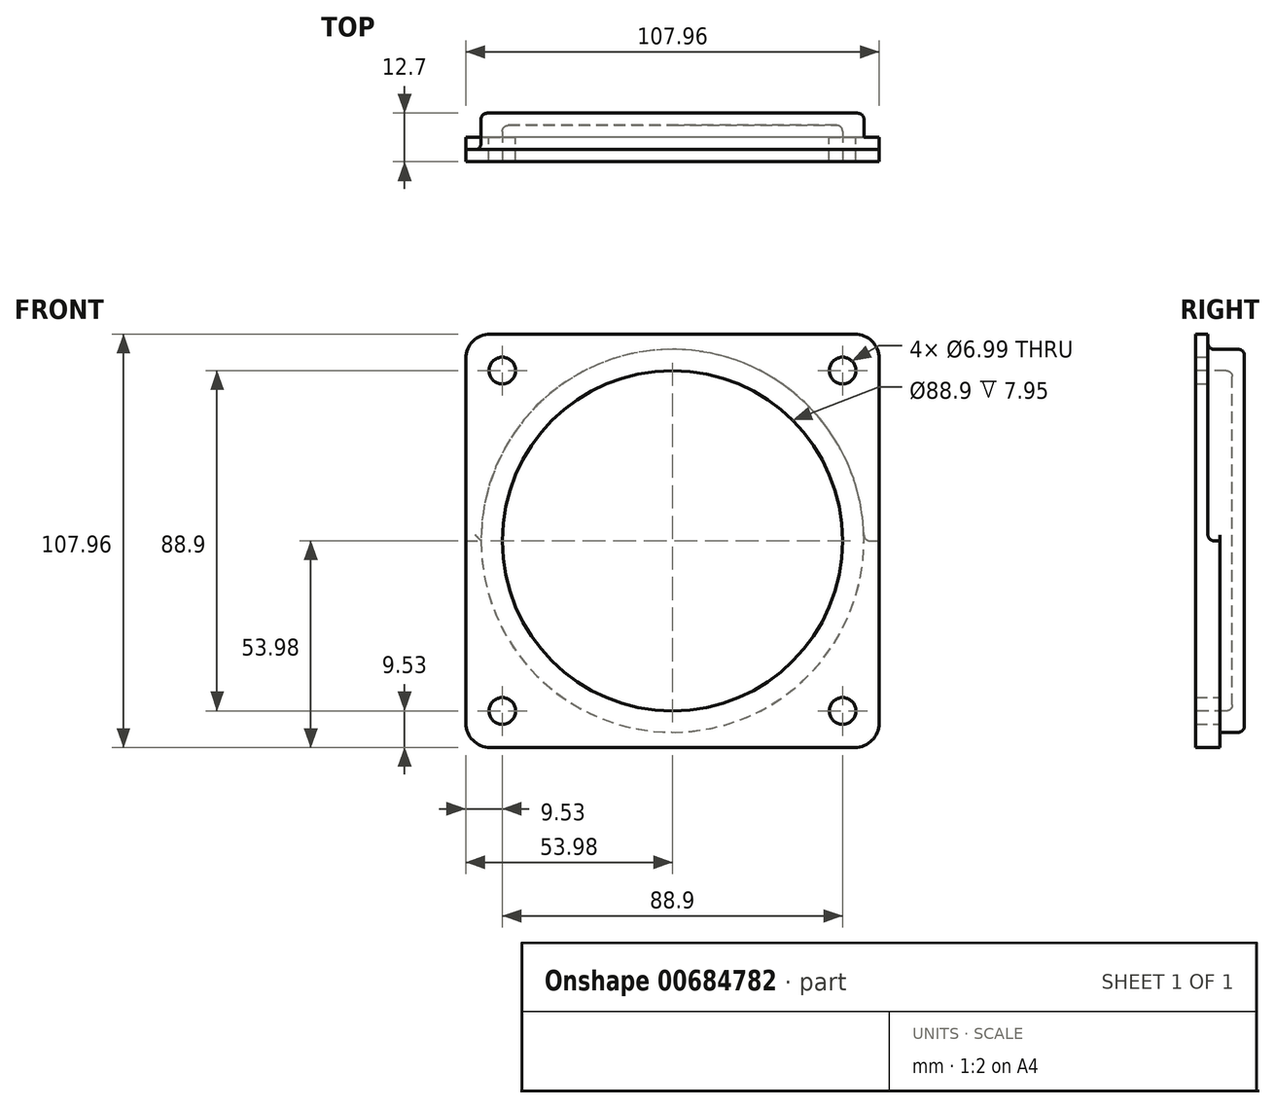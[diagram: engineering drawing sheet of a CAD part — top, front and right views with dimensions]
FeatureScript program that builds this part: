
annotation { "Feature Type Name" : "Feature", "Feature Type Description" : "" }
export const myFeature = defineFeature(function(context is Context, id is Id, definition is map)
    precondition{}
    {
        {
            var Q0;
            Q0=qCreatedBy(makeId("Front.planeOp"),FACE);
            var sketch = newSketch(context, id + "F0", { "sketchPlane" : qUnion([Q0])});
            skLineSegment(sketch, "E0.bottom", {"start": v(53.98, 53.97) * mm, "end": v(-53.98, 53.98) * mm});
            skLineSegment(sketch, "E0.top", {"start": v(53.97, -53.98) * mm, "end": v(-53.98, -53.98) * mm});
            skLineSegment(sketch, "E0.left", {"start": v(53.98, 53.97) * mm, "end": v(53.97, -53.98) * mm});
            skLineSegment(sketch, "E0.right", {"start": v(-53.97, 53.98) * mm, "end": v(-53.98, -53.97) * mm});
            skPoint(sketch, "E0.middle", {"position": v(0, 0) * mm});
            skCircle(sketch, "E1", {"center": v(44.45, 44.45) * mm, "radius": 3.5 * mm});
            skCircle(sketch, "E2", {"center": v(44.45, -44.45) * mm, "radius": 3.5 * mm});
            skCircle(sketch, "E3.MirrorC", {"center": v(-44.45, 44.45) * mm, "radius": 3.5 * mm});
            skCircle(sketch, "E4.MirrorC", {"center": v(-44.45, -44.45) * mm, "radius": 3.5 * mm});
            skSolve(sketch);
        }
        {
            var Q0;
            Q0 = qSketchRegion(id + "F0", true);
            extrude(context, id + "F1", {"entities" : qUnion([Q0]), "depth" : 6.35 * mm, "offsetDistance" : 25.4 * mm});
        }
        {
            var Q0;
            Q0=makeQuery(id+"F1.opExtrude","CAP_FACE",FACE,{"disambiguationData":[OSD([sQuery(id+"F0.wireOp",EDGE,"E0.bottom"),sQuery(id+"F0.wireOp",EDGE,"E0.top"),sQuery(id+"F0.wireOp",EDGE,"E0.left"),sQuery(id+"F0.wireOp",EDGE,"E0.right"),sQuery(id+"F0.wireOp",EDGE,"E1"),sQuery(id+"F0.wireOp",EDGE,"E2"),sQuery(id+"F0.wireOp",EDGE,"E3.MirrorC"),sQuery(id+"F0.wireOp",EDGE,"E4.MirrorC")])],"isStart":true});
            var sketch = newSketch(context, id + "F2", { "sketchPlane" : qUnion([Q0])});
            skCircle(sketch, "E5", {"center": v(0, 0) * mm, "radius": 50.01 * mm});
            skSolve(sketch);
        }
        {
            var Q0;
            Q0 = qSketchRegion(id + "F2", true);
            extrude(context, id + "F3", {"entities" : qUnion([Q0]), "operationType" : NewBodyOperationType.ADD, "depth" : 6.35 * mm, "offsetDistance" : 25.4 * mm});
        }
        {
            var Q0;
            Q0=makeQuery(id+"F1.opExtrude","CAP_FACE",FACE,{"disambiguationData":[OSD([sQuery(id+"F0.wireOp",EDGE,"E0.bottom"),sQuery(id+"F0.wireOp",EDGE,"E0.top"),sQuery(id+"F0.wireOp",EDGE,"E0.left"),sQuery(id+"F0.wireOp",EDGE,"E0.right"),sQuery(id+"F0.wireOp",EDGE,"E1"),sQuery(id+"F0.wireOp",EDGE,"E2"),sQuery(id+"F0.wireOp",EDGE,"E3.MirrorC"),sQuery(id+"F0.wireOp",EDGE,"E4.MirrorC")])],"isStart":false});
            var sketch = newSketch(context, id + "F4", { "sketchPlane" : qUnion([Q0])});
            skCircle(sketch, "E6", {"center": v(0, 0) * mm, "radius": 44.45 * mm});
            skSolve(sketch);
        }
        {
            var Q0;
            Q0 = qSketchRegion(id + "F4", true);
            extrude(context, id + "F5", {"entities" : qUnion([Q0]), "operationType" : NewBodyOperationType.REMOVE, "oppositeDirection" : true, "depth" : 9.52 * mm, "offsetDistance" : 25.4 * mm});
        }
        {
            var Q0;
            Q0=makeQuery(id+"F1.opExtrude","CAP_FACE",FACE,{"disambiguationData":[OSD([sQuery(id+"F0.wireOp",EDGE,"E0.bottom"),sQuery(id+"F0.wireOp",EDGE,"E0.top"),sQuery(id+"F0.wireOp",EDGE,"E0.left"),sQuery(id+"F0.wireOp",EDGE,"E0.right"),sQuery(id+"F0.wireOp",EDGE,"E1"),sQuery(id+"F0.wireOp",EDGE,"E2"),sQuery(id+"F0.wireOp",EDGE,"E3.MirrorC"),sQuery(id+"F0.wireOp",EDGE,"E4.MirrorC")])],"isStart":true});
            var sketch = newSketch(context, id + "F6", { "sketchPlane" : qUnion([Q0])});
            skArc(sketch, "E7", {"start": v(50.01, 0) * mm, "mid": v(0, 50.01) * mm, "end": v(-50.01, 0) * mm});
            skLineSegment(sketch, "E8", {"start": v(-50.01, 0) * mm, "end": v(-53.97, 0) * mm});
            skLineSegment(sketch, "E9", {"start": v(-53.97, 0) * mm, "end": v(-53.98, 53.97) * mm});
            skLineSegment(sketch, "E10", {"start": v(-53.98, 53.97) * mm, "end": v(53.97, 53.98) * mm});
            skLineSegment(sketch, "E11", {"start": v(53.97, 53.98) * mm, "end": v(53.98, 0) * mm});
            skLineSegment(sketch, "E12", {"start": v(53.98, 0) * mm, "end": v(50.01, 0) * mm});
            skSolve(sketch);
        }
        {
            var Q0;
            Q0=makeQuery(id+"F6.imprint","IMPRINT",FACE,{"disambiguationData":[TD([[makeQuery(id+"F6.imprint","IMPRINT",EDGE,{"derivedFrom":sQuery(id+"F6.wireOp",EDGE,"E7")}),-1.0]])]});
            extrude(context, id + "F7", {"entities" : qUnion([Q0]), "operationType" : NewBodyOperationType.REMOVE, "oppositeDirection" : true, "depth" : 3.17 * mm, "offsetDistance" : 25.4 * mm});
        }
        {
            var Q0;
            Q0=makeQuery(id+"F5.boolean.opBoolean","COPY",EDGE,{"derivedFrom":makeQuery(id+"F5.opExtrude","CAP_EDGE",EDGE,{"disambiguationData":[OSD([sQuery(id+"F4.wireOp",EDGE,"E6")])],"isStart":false})});
            var Q1;
            Q1=makeQuery(id+"F5.boolean.opBoolean","COPY",EDGE,{"derivedFrom":makeQuery(id+"F5.opExtrude","CAP_EDGE",EDGE,{"disambiguationData":[OSD([sQuery(id+"F4.wireOp",EDGE,"E6")])],"isStart":true})});
            var Q2;
            Q2=makeQuery(id+"F3.opExtrude","CAP_EDGE",EDGE,{"disambiguationData":[OSD([sQuery(id+"F2.wireOp",EDGE,"E5")])],"isStart":false});
            var Q3;
            Q3=makeQuery(id+"F3.opExtrude","CAP_EDGE",EDGE,{"disambiguationData":[OSD([sQuery(id+"F2.wireOp",EDGE,"E5")])],"isStart":true});
            var Q4;
            Q4=makeQuery(id+"F7.boolean.opBoolean","COPY",EDGE,{"derivedFrom":makeQuery(id+"F7.opExtrude","CAP_EDGE",EDGE,{"disambiguationData":[OSD([sQuery(id+"F6.wireOp",EDGE,"E12")])],"isStart":false})});
            var Q5;
            Q5=makeQuery(id+"F7.boolean.opBoolean","COPY",EDGE,{"derivedFrom":makeQuery(id+"F7.opExtrude","CAP_EDGE",EDGE,{"disambiguationData":[OSD([sQuery(id+"F6.wireOp",EDGE,"E12")])],"isStart":true})});
            var Q6;
            Q6=makeQuery(id+"F7.boolean.opBoolean","COPY",EDGE,{"derivedFrom":makeQuery(id+"F7.opExtrude","CAP_EDGE",EDGE,{"disambiguationData":[OSD([sQuery(id+"F6.wireOp",EDGE,"E7")])],"isStart":false})});
            var Q7;
            Q7=makeQuery(id+"F7.boolean.opBoolean","COPY",EDGE,{"derivedFrom":makeQuery(id+"F7.opExtrude","CAP_EDGE",EDGE,{"disambiguationData":[OSD([sQuery(id+"F6.wireOp",EDGE,"E8")])],"isStart":false})});
            var Q8;
            Q8=makeQuery(id+"F7.boolean.opBoolean","COPY",EDGE,{"derivedFrom":makeQuery(id+"F7.opExtrude","SWEPT_EDGE",EDGE,{"disambiguationData":[OSD([sQuery(id+"F2.wireOp",EDGE,"E5"),sQuery(id+"F6.wireOp",EDGE,"E7"),sQuery(id+"F6.wireOp",EDGE,"E8")])]})});
            fillet(context, id + "F8", {"entities" : qUnion([Q0, Q1, Q2, Q3, Q4, Q5, Q6, Q7, Q8]), "radius" : 1.57 * mm, "tangentPropagation" : true, "allowEdgeOverflow" : false});
        }
        {
            var Q0;
            Q0=makeQuery(id+"F1.opExtrude","SWEPT_EDGE",EDGE,{"disambiguationData":[OSD([sQuery(id+"F0.wireOp",EDGE,"E0.bottom"),sQuery(id+"F0.wireOp",EDGE,"E0.right")])]});
            var Q1;
            Q1=makeQuery(id+"F1.opExtrude","SWEPT_EDGE",EDGE,{"disambiguationData":[OSD([sQuery(id+"F0.wireOp",EDGE,"E0.top"),sQuery(id+"F0.wireOp",EDGE,"E0.right")])]});
            var Q2;
            Q2=makeQuery(id+"F1.opExtrude","SWEPT_EDGE",EDGE,{"disambiguationData":[OSD([sQuery(id+"F0.wireOp",EDGE,"E0.top"),sQuery(id+"F0.wireOp",EDGE,"E0.left")])]});
            var Q3;
            Q3=makeQuery(id+"F1.opExtrude","SWEPT_EDGE",EDGE,{"disambiguationData":[OSD([sQuery(id+"F0.wireOp",EDGE,"E0.bottom"),sQuery(id+"F0.wireOp",EDGE,"E0.left")])]});
            fillet(context, id + "F9", {"entities" : qUnion([Q0, Q1, Q2, Q3]), "radius" : 6.35 * mm, "tangentPropagation" : true, "allowEdgeOverflow" : false});
        }
    });
